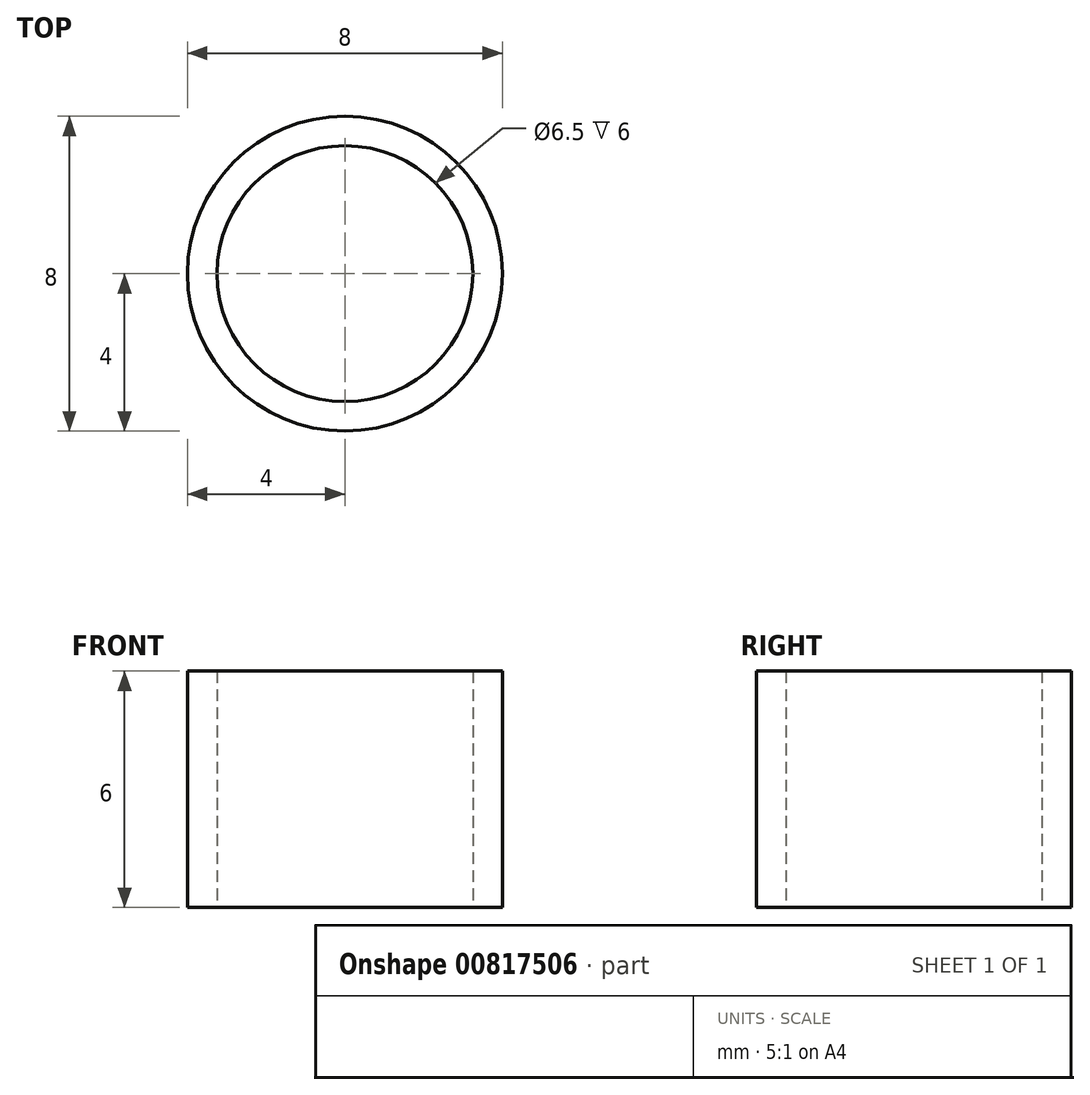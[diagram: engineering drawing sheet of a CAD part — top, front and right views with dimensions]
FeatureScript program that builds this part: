
annotation { "Feature Type Name" : "Feature", "Feature Type Description" : "" }
export const myFeature = defineFeature(function(context is Context, id is Id, definition is map)
    precondition{}
    {
        {
            var Q0;
            Q0=qCreatedBy(makeId("Top.planeOp"),FACE);
            var sketch = newSketch(context, id + "F0", { "sketchPlane" : qUnion([Q0])});
            skCircle(sketch, "E0", {"center": v(0, 0) * mm, "radius": 4 * mm});
            skCircle(sketch, "E1", {"center": v(0, 0) * mm, "radius": 3.25 * mm});
            skSolve(sketch);
        }
        {
            var Q0;
            Q0=makeQuery(id+"F0.imprint","IMPRINT",FACE,{"disambiguationData":[TD([[makeQuery(id+"F0.imprint","IMPRINT",EDGE,{"derivedFrom":sQuery(id+"F0.wireOp",EDGE,"E0")}),1.0]])]});
            extrude(context, id + "F1", {"entities" : qUnion([Q0]), "depth" : 6 * mm, "offsetDistance" : 25 * mm});
        }
    });
